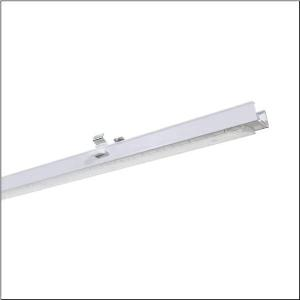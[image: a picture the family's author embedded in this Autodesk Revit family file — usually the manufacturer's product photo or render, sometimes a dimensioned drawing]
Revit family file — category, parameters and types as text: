
# Revit family: trunking_flex_31_51re18ma46b
name_source: partatom
category: Lighting Fixtures
units: mm (PartAtom-declared; Revit-internal decimal feet)

## family parameters
Cut with Voids When Loaded = No
Host = Face
Light Source = No
Part Type = Normal
Room Calculation Point = No
Round Connector Dimension = Use Diameter
Shared = No

## types (1)
- --- (1 x LED, 6400 lm, 40 W, 4000K)
    Apparent Load = 40 VA
    CIE Flux Codes = 71 89 97 97 100
    Color Rendering = 80
    Color Temperature = 4000K
    Default Elevation = 1800 mm
    Description = Trunking Flex 31, luminaire insert, of extruded aluminium section, coated, traffic white (RAL 9016), length: 1.172mm, width: 91mm, height: 53mm, LED rated luminous flux: 6.400lm, light colour: 840, SDCM (Standard Deviation of Colour Matching)MacAdam ≤ 3 SDCM (initial), control gear: ON/OFF Multilumen, with system connector: socket, mains connection: 220..240V, AC, 50/60Hz, rated input power: 40W, luminous flux adjustable on luminaire in four steps (3420/4540/5580/6630lm), connected load according to luminous flux setting (20/26/33/40W), primary light control with lens, of plastic, primary optical cover: cover, of PMMA, light emission: direct distribution, protection rating (complete): IP20, insulation class (complete): insulation class I (protective earthing), certification: CE, UKCA, impact resistance: IK02, permissible ambient temperature for indoor applications: -20..+40°C, packaging unit: 1 piece
    Height = 58 mm
    Lamp = 1 x LED
    Lamp Light Flux = 6400 lm
    Lamp Power = 40 W
    Lamp count = 1
    Length = 1172 mm
    Luminous efficacy = 160 lm/W
    Manufacturer = Siteco
    ModVariant = No
    Model = 51RE18MA46B
    Mounting Place = Ceiling
    Mounting Type = Pendant
    Number of Poles = 1
    OnlyDefault = Yes
    Power Factor = 1
    Product Name = Trunking Flex 31
    Product group = luminaire insert | ceiling pendant
    ProductGroupID = 901
    Protection Class = Protection class I
    Protection Degree = IP 20
    RLX_Detail_Level = 1
    RLX_Emergency_Light_Flux = 0 lm
    RLX_Emergency_Type = 0
    RLX_Emergency_Type_DB = No
    RlxData = <blob elided: 20157 chars, md5=de3ef96e>
    Socket = socket
    Standby Power = 0 W
    System Light Flux = 6400 lm
    System Power = 40 W
    Type Comments = factory setting: luminous flux: 100 % | (ON | ON) | 300 mA
    Type Image = l_1266702.jpg
    URL = http://relux.com
    VarID = @adj_067067
    Voltage = 0 V
    Weight = 0.00 kg
    Width = 65 mm

## geometry (parser evidence)
native form markers: Blend x4, Sweep x11
no freeform markers — native parametric forms only
